# Revit family: Worksurface-Teknion-HWBWJT_hiSpace_120_Worksurface_With_Radius_Corners-R2020
name_source: partatom
category: Furniture
units: mm (PartAtom-declared; Revit-internal decimal feet)

## family parameters
Always vertical = Yes
Cut with Voids When Loaded = No
OmniClass Number = 23.40.20.00
OmniClass Title = General Furniture and Specialties
Room Calculation Point = No
Shared = No
Work Plane-Based = No

## types (6) — shared parameters
Available Depth = 23 & 29 Inch
Available Width = 46, 52 & 58 Inch
Manufacturer = Teknion
Manufacturer Fax = 416.661.4586
Part Number = HWBWJT
Product Documentation Link = https://www.teknion.com
Product Line = hiSpace 120 Bench
Product Page URL = https://www.teknion.com
Series = Height-Adjustable Bench hiSpace
URL = www.teknion.com
Warranty = http://www.teknion.com
zero-valued in all types: Default Elevation

## per-type parameters (varying)
| type | Actual Depth | Actual Width | Depth | Description | Model | Width | Width A |
| 29" Depth, 58" Width | 28.5 " | 58.259 " | 29 " | hiSpace 120 Worksurface With Radius Corners - 29" Depth, 58" Width | HWBWJT2958 | 58 " | 24.484 " |
| 23" Depth, 46" Width | 22.5 " | 46.259 " | 23 " | hiSpace 120 Worksurface With Radius Corners - 23" Depth, 46" Width | HWBWJT2346 | 46 " | 15.948 " |
| 29" Depth, 52" Width | 28.5 " | 52.259 " | 29 " | hiSpace 120 Worksurface With Radius Corners - 29" Depth, 52" Width | HWBWJT2952 | 52 " | 18.484 " |
| 29" Depth, 46" Width | 28.5 " | 46.259 " | 29 " | hiSpace 120 Worksurface With Radius Corners - 29" Depth, 46" Width | HWBWJT2946 | 46 " | 12.484 " |
| 23" Depth, 52" Width | 22.5 " | 52.259 " | 23 " | hiSpace 120 Worksurface With Radius Corners - 23" Depth, 52" Width | HWBWJT2352 | 52 " | 21.948 " |
| 23" Depth, 58" Width | 22.5 " | 58.259 " | 23 " | hiSpace 120 Worksurface With Radius Corners - 23" Depth, 58" Width | HWBWJT2358 | 58 " | 27.948 " |

## geometry (parser evidence)
native form markers: Sweep x4
no freeform markers — native parametric forms only
